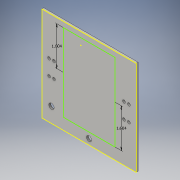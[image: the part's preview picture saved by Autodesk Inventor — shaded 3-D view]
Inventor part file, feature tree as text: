
AUTODESK INVENTOR PART (.ipt)
format: ipt  version: 2016 (Build 200138000, 138)  size: 131,072 bytes
history: native  units: in
note: dims shown in document units (in); Inventor stores cm internally (conversion verified against a paired STEP export)
features: sketch x5, extrude x4
ambient origin geometry x8: Origin, YZ Plane, XZ Plane, XY Plane, X Axis, Y Axis, Z Axis, Center Point
bodies: Solid1 (feature_tree)
feature tree (9):
  extrude  "Extrusion1"  Depth=3.9in
  sketch  "Sketch5"  dims[d2=0.08in d3=0.0in d14=1.6035in]
  extrude  "Extrusion8"  Depth=0.08in
  extrude  "Extrusion9"  Depth=0.213in
  extrude  "Extrusion11"  Depth=0.223in
  sketch  "Sketch1"  dims[d0=3.9in d1=3.9in]
  sketch  "Sketch9"  dims[d15=1.6035in d28=0.213in]
  sketch  "Sketch10"  dims[d29=0.2in d30=0.0in d31=0.223in]
  sketch  "Sketch16"  dims[d32=0.2in d33=0.0in d50=0.119in d51=1.0in d52=0.0in]
